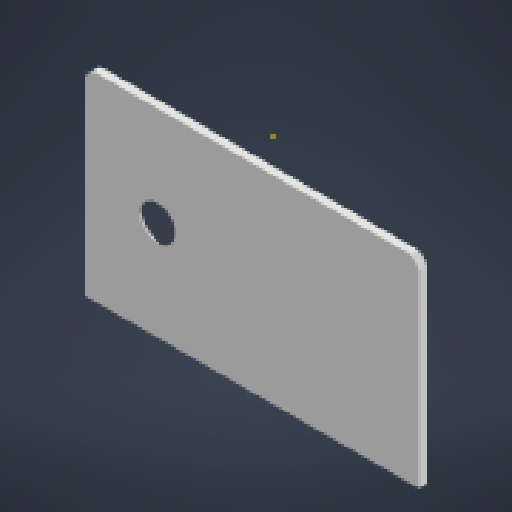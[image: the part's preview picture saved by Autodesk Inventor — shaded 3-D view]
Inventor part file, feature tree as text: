
AUTODESK INVENTOR PART (.ipt)
format: ipt  version: 2024 (Build 280153000, 153)  size: 117,248 bytes
history: native  units: mm
features: sketch x2, other x1, extrude x1
ambient origin geometry x8: Origin, YZ Plane, XZ Plane, XY Plane, X Axis, Y Axis, Z Axis, Center Point
bodies: Body1 (feature_tree)
feature tree (4):
  other  "솔리드1"
  extrude  "돌출1"  Depth=207.0mm
  sketch  "스케치2"
  sketch  "스케치1"
